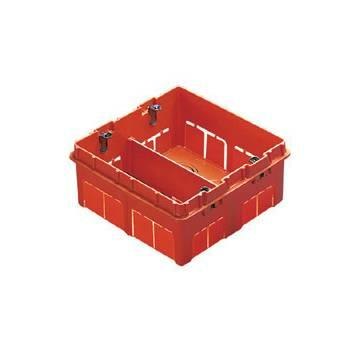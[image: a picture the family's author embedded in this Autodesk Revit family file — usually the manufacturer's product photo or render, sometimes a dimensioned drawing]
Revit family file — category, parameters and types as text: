
# Revit family: Building-FlushMountingEnclosures-GEWISS-24SC-BOXES_BIGBOX_3P+3P_4P+4P_6P+6P
name_source: partatom
category: Apparecchi elettrici
revit_build: Autodesk Revit 2016 (Build: 20161004_0715(x64)
units: mm (PartAtom-declared; Revit-internal decimal feet)

## family parameters
Condiviso = Sì
Host = Superficie
Mantenere orientamento annotazione = Sì
Numero OmniClass = 23.80.30.14.24
Punto di calcolo locali = Sì
Quota connettore circolare = Usa diametro
Taglio con vuoti quando caricato = Sì
Tipo di parte = Normale
Titolo OmniClass = Junction Boxes

## types (3) — shared parameters
Catalogue = BUILDING
Catalogue Range = 24SC
Centro viti = 107 mm
Characteristics = Halogen free
For walls = Masonry
Glow Wire Test = 650°C
IDF = ed45e5b7-06b5-4938-867e-6b93da6ef299
IDT = 9038462e-8cfc-449c-bcc0-59c396fc2d03
Immagine tipo = GW24238.jpg
Incasso = 53 mm  [stored 0.173885 ft]
Installation = Flush mounting enclosures
Operating temperature = -15 ÷ +60°C
Produttore = GEWISS S.p.A.
Prospetto di default = 45 mm
SEO = Box
Scatola GW24206 = Sì
Technical sheet = https://www.gewiss.com
Thermo-pressure with ball = 70
Type: = High capacity
URL = https://www.gewiss.com
Version file RFA = 19.0

## per-type parameters (varying)
| type | Compartment pre-arrangement | Description: | Descrizione | EAN code | Electrocod | Fixing supports axles distance | Modello | No. SYSTEM modules | Outer dim. LxHxD (mm) | Type of material |
| GW24237 - Box 8P (4+4) | 2 | 8 gang (4+4) | 8 GANG F.M.BOX W.METAL FIXING SUPP. | 8011564024984 | 0110 | 108,5MM | GW24237 | 8 gang (4+4) | 131x129x53 | Halogen free with Standard EN 50267-2-2 |
| GW24206 - Box 6P (3+3) | 1 | 6 gang (3+3) | 6 GANG(3+3) F.M.BOX W.METAL FIXING SUPP. | 8011564016637 | 0210 | 83,5MM | GW24206 | 6 gang (3+3) | 108x124x50 | Halogen-free in compliance with EN 60754-2 |
| GW24238 - Box 12P (6+6) | 2 | 12 gang (6+6) | 12 GANG F.M.BOX W.METAL FIXING SUPP. | 8011564024991 | 0110 | 163,5MM | GW24238 | 12 gang (6+6) | 186x132x53 | Halogen-free in compliance with EN 60754-2 |

note: source unit labels omitted for Thermo-pressure with ball — the stored unit's dimension contradicts the parameter name (converter mislabeling)

note: [stored X ft] marks values corroborated as IEEE doubles in the binary element streams (Revit-internal decimal feet)

## geometry (parser evidence)
native form markers: Blend x4
no freeform markers — native parametric forms only
